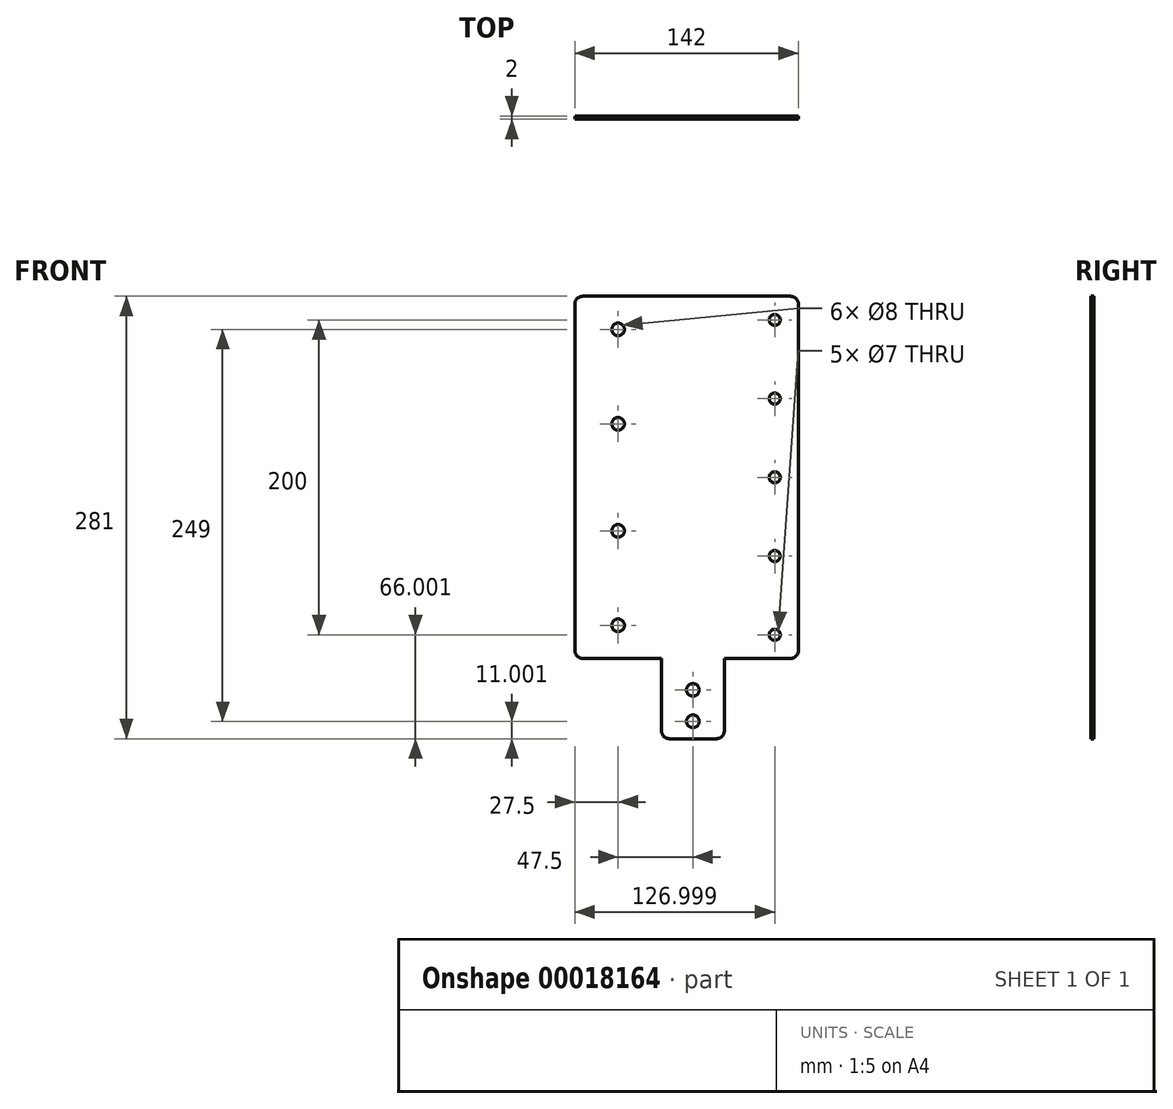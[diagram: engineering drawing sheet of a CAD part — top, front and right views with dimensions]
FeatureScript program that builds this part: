
annotation { "Feature Type Name" : "Feature", "Feature Type Description" : "" }
export const myFeature = defineFeature(function(context is Context, id is Id, definition is map)
    precondition{}
    {
        {
            var Q0;
            Q0=qCreatedBy(makeId("Front.planeOp"),FACE);
            var sketch = newSketch(context, id + "F0", { "sketchPlane" : qUnion([Q0])});
            skLineSegment(sketch, "E0.bottom", {"start": v(68.23, -76.43) * mm, "end": v(23.23, -76.43) * mm});
            skLineSegment(sketch, "E0.top", {"start": v(68.23, 153.57) * mm, "end": v(23.23, 153.57) * mm});
            skLineSegment(sketch, "E0.right", {"start": v(18.23, -71.43) * mm, "end": v(18.23, 148.57) * mm});
            skLineSegment(sketch, "E1", {"start": v(-30.15, 38.57) * mm, "end": v(-175.04, 38.57) * mm, "construction": true});
            skPoint(sketch, "E2.visualSharp", {"position": v(18.23, 153.57) * mm});
            skArc(sketch, "E2.filletArc", {"start": v(23.23, 153.57) * mm, "mid": v(19.7, 152.1) * mm, "end": v(18.23, 148.57) * mm});
            skPoint(sketch, "E3.visualSharp", {"position": v(18.23, -76.43) * mm});
            skArc(sketch, "E3.filletArc", {"start": v(18.23, -71.43) * mm, "mid": v(19.7, -74.96) * mm, "end": v(23.23, -76.43) * mm});
            skLineSegment(sketch, "E4", {"start": v(45.73, 153.57) * mm, "end": v(45.73, -76.43) * mm, "construction": true});
            skCircle(sketch, "E5", {"center": v(45.73, 72.57) * mm, "radius": 4 * mm});
            skCircle(sketch, "E6", {"center": v(45.73, 132.57) * mm, "radius": 4 * mm});
            skCircle(sketch, "E7.MirrorC", {"center": v(45.73, 4.57) * mm, "radius": 4 * mm});
            skCircle(sketch, "E8.MirrorC", {"center": v(45.73, -55.43) * mm, "radius": 4 * mm});
            skLineSegment(sketch, "E9.bottom", {"start": v(73.23, -76.43) * mm, "end": v(73.23, -122.43) * mm});
            skLineSegment(sketch, "E9.top", {"start": v(113.23, -76.43) * mm, "end": v(113.23, -122.43) * mm});
            skLineSegment(sketch, "E9.right", {"start": v(78.23, -127.43) * mm, "end": v(108.23, -127.43) * mm});
            skPoint(sketch, "E10.visualSharp", {"position": v(73.23, -127.43) * mm});
            skArc(sketch, "E10.filletArc", {"start": v(73.23, -122.43) * mm, "mid": v(74.7, -125.96) * mm, "end": v(78.23, -127.43) * mm});
            skPoint(sketch, "E11.visualSharp", {"position": v(113.23, -127.43) * mm});
            skArc(sketch, "E11.filletArc", {"start": v(108.23, -127.43) * mm, "mid": v(111.77, -125.96) * mm, "end": v(113.23, -122.43) * mm});
            skCircle(sketch, "E12", {"center": v(93.23, -96.43) * mm, "radius": 4 * mm});
            skCircle(sketch, "E13", {"center": v(93.23, -116.43) * mm, "radius": 4 * mm});
            skLineSegment(sketch, "E14", {"start": v(93.23, -127.43) * mm, "end": v(93.23, -76.16) * mm, "construction": true});
            skLineSegment(sketch, "E15", {"start": v(68.23, 153.57) * mm, "end": v(120.23, 153.57) * mm});
            skCircle(sketch, "E16.MirrorC", {"center": v(145.23, -61.43) * mm, "radius": 3.5 * mm});
            skArc(sketch, "E17.MirrorCS", {"start": v(155.23, 153.57) * mm, "mid": v(158.77, 152.1) * mm, "end": v(160.23, 148.57) * mm});
            skArc(sketch, "E18.MirrorCS", {"start": v(160.23, -71.43) * mm, "mid": v(158.77, -74.96) * mm, "end": v(155.23, -76.43) * mm});
            skCircle(sketch, "E19.MirrorC", {"center": v(145.23, 138.57) * mm, "radius": 3.5 * mm});
            skCircle(sketch, "E20.MirrorC", {"center": v(145.23, 38.57) * mm, "radius": 3.5 * mm});
            skPoint(sketch, "E21.MirrorP", {"position": v(160.23, 153.57) * mm});
            skCircle(sketch, "E22.MirrorC", {"center": v(145.23, 88.57) * mm, "radius": 3.5 * mm});
            skCircle(sketch, "E23.MirrorC", {"center": v(145.23, -11.43) * mm, "radius": 3.5 * mm});
            skLineSegment(sketch, "E24.MirrorCS", {"start": v(113.23, -76.43) * mm, "end": v(155.23, -76.43) * mm});
            skLineSegment(sketch, "E25.MirrorCS", {"start": v(145.23, 140.53) * mm, "end": v(145.23, -82.44) * mm, "construction": true});
            skLineSegment(sketch, "E26.MirrorCS", {"start": v(160.23, -71.43) * mm, "end": v(160.23, 148.57) * mm});
            skLineSegment(sketch, "E27.MirrorCS", {"start": v(145.23, -61.43) * mm, "end": v(128.9, -61.43) * mm, "construction": true});
            skLineSegment(sketch, "E28.MirrorCS", {"start": v(120.23, 153.57) * mm, "end": v(155.23, 153.57) * mm});
            skPoint(sketch, "E29.MirrorP", {"position": v(160.23, -76.43) * mm});
            skLineSegment(sketch, "E30.MirrorCS", {"start": v(160.23, 38.57) * mm, "end": v(120.23, 38.57) * mm, "construction": true});
            skLineSegment(sketch, "E31.MirrorCS", {"start": v(145.23, -61.43) * mm, "end": v(145.23, -11.43) * mm, "construction": true});
            skLineSegment(sketch, "E32", {"start": v(68.23, -76.43) * mm, "end": v(73.23, -76.43) * mm});
            skSolve(sketch);
        }
        {
            var Q0;
            Q0 = qSketchRegion(id + "F0", true);
            extrude(context, id + "F1", {"entities" : qUnion([Q0]), "depth" : 2 * mm});
        }
    });
